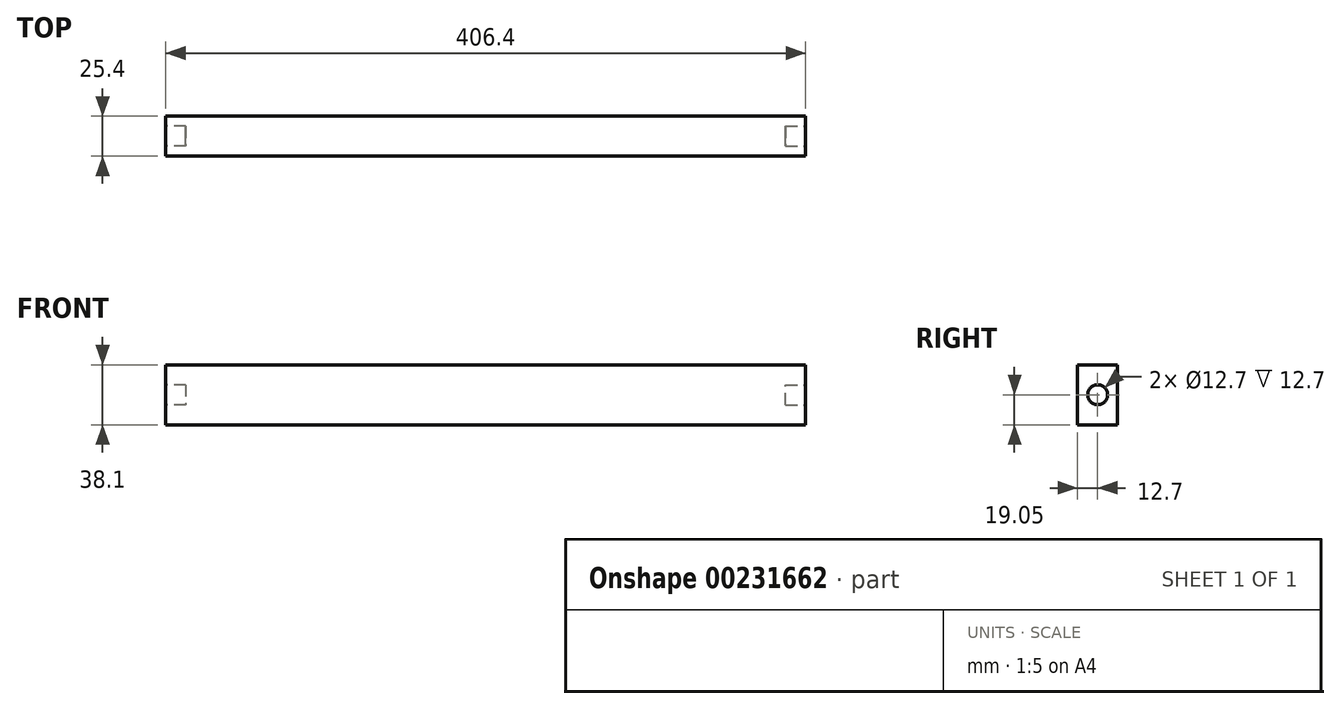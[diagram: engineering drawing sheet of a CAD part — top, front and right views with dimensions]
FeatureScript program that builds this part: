
annotation { "Feature Type Name" : "Feature", "Feature Type Description" : "" }
export const myFeature = defineFeature(function(context is Context, id is Id, definition is map)
    precondition{}
    {
        {
            var Q0;
            Q0=qCreatedBy(makeId("Front.planeOp"),FACE);
            var sketch = newSketch(context, id + "F0", { "sketchPlane" : qUnion([Q0])});
            skLineSegment(sketch, "E0.bottom", {"start": v(-203.2, 19.05) * mm, "end": v(203.2, 19.05) * mm});
            skLineSegment(sketch, "E0.top", {"start": v(-203.2, -19.05) * mm, "end": v(203.2, -19.05) * mm});
            skLineSegment(sketch, "E0.left", {"start": v(-203.2, 19.05) * mm, "end": v(-203.2, -19.05) * mm});
            skLineSegment(sketch, "E0.right", {"start": v(203.2, 19.05) * mm, "end": v(203.2, -19.05) * mm});
            skPoint(sketch, "E0.middle", {"position": v(0, 0) * mm});
            skSolve(sketch);
        }
        {
            var Q0;
            Q0 = qSketchRegion(id + "F0", true);
            extrude(context, id + "F1", {"entities" : qUnion([Q0]), "depth" : 25.4 * mm});
        }
        {
            var Q0;
            Q0=makeQuery(id+"F1.opExtrude","SWEPT_FACE",FACE,{"disambiguationData":[OSD([sQuery(id+"F0.wireOp",EDGE,"E0.left")])]});
            var sketch = newSketch(context, id + "F2", { "sketchPlane" : qUnion([Q0])});
            skLineSegment(sketch, "E1", {"start": v(0, 19.05) * mm, "end": v(25.4, -19.05) * mm, "construction": true});
            skLineSegment(sketch, "E2", {"start": v(25.4, -19.05) * mm, "end": v(0, -19.05) * mm, "construction": true});
            skLineSegment(sketch, "E3", {"start": v(0, -19.05) * mm, "end": v(25.4, 19.05) * mm, "construction": true});
            skCircle(sketch, "E4", {"center": v(12.7, 0) * mm, "radius": 6.35 * mm});
            skSolve(sketch);
        }
        {
            var Q0;
            Q0 = qSketchRegion(id + "F2", true);
            extrude(context, id + "F3", {"entities" : qUnion([Q0]), "operationType" : NewBodyOperationType.REMOVE, "oppositeDirection" : true, "depth" : 12.7 * mm});
        }
        {
            var Q0;
            Q0=makeQuery(id+"F1.opExtrude","SWEPT_FACE",FACE,{"disambiguationData":[OSD([sQuery(id+"F0.wireOp",EDGE,"E0.right")])]});
            var sketch = newSketch(context, id + "F4", { "sketchPlane" : qUnion([Q0])});
            skLineSegment(sketch, "E5", {"start": v(-25.4, 19.05) * mm, "end": v(0, -19.05) * mm, "construction": true});
            skLineSegment(sketch, "E6", {"start": v(0, -19.05) * mm, "end": v(-25.4, -19.05) * mm, "construction": true});
            skLineSegment(sketch, "E7", {"start": v(-25.4, -19.05) * mm, "end": v(0, 19.05) * mm, "construction": true});
            skCircle(sketch, "E8", {"center": v(-12.7, 0) * mm, "radius": 6.35 * mm});
            skSolve(sketch);
        }
        {
            var Q0;
            Q0 = qSketchRegion(id + "F4", true);
            extrude(context, id + "F5", {"entities" : qUnion([Q0]), "operationType" : NewBodyOperationType.REMOVE, "oppositeDirection" : true, "depth" : 12.7 * mm});
        }
    });
